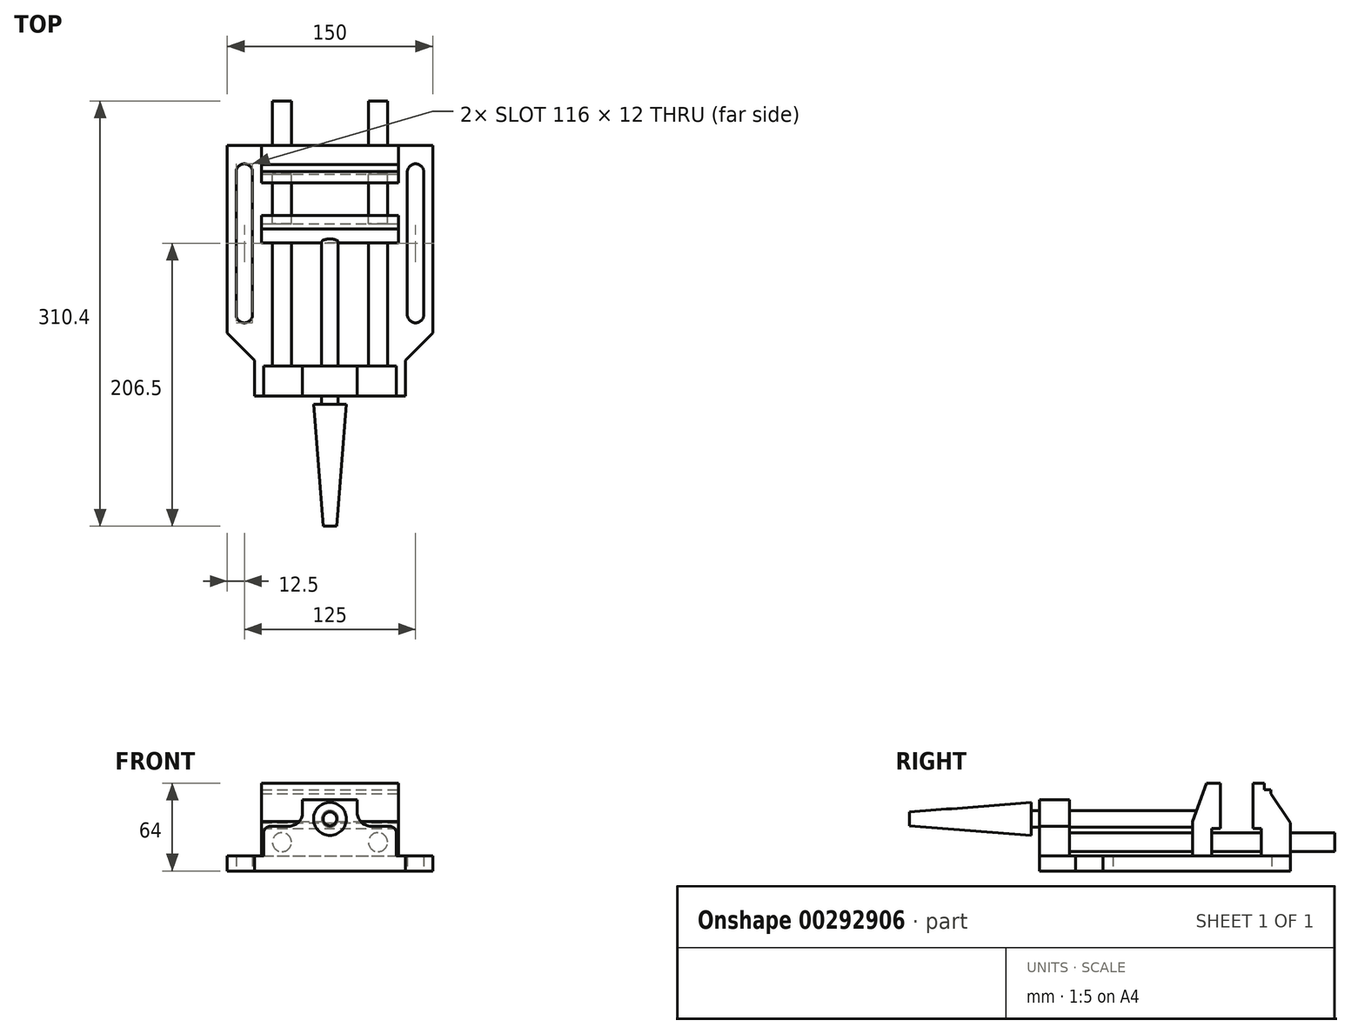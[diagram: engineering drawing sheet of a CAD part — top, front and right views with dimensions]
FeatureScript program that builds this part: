
annotation { "Feature Type Name" : "Feature", "Feature Type Description" : "" }
export const myFeature = defineFeature(function(context is Context, id is Id, definition is map)
    precondition{}
    {
        {
            var Q0;
            Q0=qCreatedBy(makeId("Top.planeOp"),FACE);
            var sketch = newSketch(context, id + "F0", { "sketchPlane" : qUnion([Q0])});
            skLineSegment(sketch, "E0", {"start": v(0, 0) * mm, "end": v(0, 26.2) * mm});
            skLineSegment(sketch, "E1", {"start": v(0, 26.2) * mm, "end": v(20, 46.2) * mm});
            skLineSegment(sketch, "E2", {"start": v(20, 46.2) * mm, "end": v(20, 183) * mm});
            skLineSegment(sketch, "E3", {"start": v(20, 183) * mm, "end": v(-55, 183) * mm});
            skLineSegment(sketch, "E4", {"start": v(-55, 183) * mm, "end": v(-55, 0) * mm});
            skLineSegment(sketch, "E5", {"start": v(-55, 0) * mm, "end": v(0, 0) * mm});
            skLineSegment(sketch, "E6", {"start": v(13.5, 59.5) * mm, "end": v(13.5, 163.5) * mm});
            skArc(sketch, "E7", {"start": v(13.5, 163.5) * mm, "mid": v(7.5, 169.5) * mm, "end": v(1.5, 163.5) * mm});
            skLineSegment(sketch, "E8", {"start": v(1.5, 59.5) * mm, "end": v(1.5, 163.5) * mm});
            skArc(sketch, "E9", {"start": v(1.5, 59.5) * mm, "mid": v(7.5, 53.5) * mm, "end": v(13.5, 59.5) * mm});
            skSolve(sketch);
        }
        {
            var Q0;
            Q0=makeQuery(id+"F0.imprint","IMPRINT",FACE,{"disambiguationData":[TD([[makeQuery(id+"F0.imprint","IMPRINT",EDGE,{"derivedFrom":sQuery(id+"F0.wireOp",EDGE,"E0")}),1.0]])]});
            extrude(context, id + "F1", {"entities" : qUnion([Q0]), "depth" : 11 * mm});
        }
        {
            var Q0;
            Q0=makeQuery(id+"F1.opExtrude","SWEPT_BODY",BODY,{"disambiguationData":[OSD([sQuery(id+"F0.wireOp",EDGE,"E0"),sQuery(id+"F0.wireOp",EDGE,"E1"),sQuery(id+"F0.wireOp",EDGE,"E2"),sQuery(id+"F0.wireOp",EDGE,"E3"),sQuery(id+"F0.wireOp",EDGE,"E4"),sQuery(id+"F0.wireOp",EDGE,"E5"),sQuery(id+"F0.wireOp",EDGE,"E6"),sQuery(id+"F0.wireOp",EDGE,"E7"),sQuery(id+"F0.wireOp",EDGE,"E8"),sQuery(id+"F0.wireOp",EDGE,"E9")])]});
            var Q1;
            Q1=makeQuery(id+"F1.opExtrude","SWEPT_FACE",FACE,{"disambiguationData":[OSD([sQuery(id+"F0.wireOp",EDGE,"E4")])]});
            mirror(context, id + "F2", {"operationType" : NewBodyOperationType.ADD, "entities" : qUnion([Q0]), "mirrorPlane" : qUnion([Q1])});
        }
        {
            var Q0;
            {var subQ0=makeQuery(id+"F1.opExtrude","SWEPT_FACE",FACE,{"disambiguationData":[OSD([sQuery(id+"F0.wireOp",EDGE,"E5")])]});Q0=makeQuery(id+"F2.boolean.opBoolean","MERGE",FACE,{"derivedFrom":[subQ0,makeQuery(id+"F2.opPattern","COPY",FACE,{"derivedFrom":subQ0,"instanceName":"1"})]});}
            var sketch = newSketch(context, id + "F3", { "sketchPlane" : qUnion([Q0])});
            skLineSegment(sketch, "E10", {"start": v(-103.5, 0) * mm, "end": v(-6.5, 0) * mm});
            skLineSegment(sketch, "E11", {"start": v(-6.5, 0) * mm, "end": v(-6.5, 27.6) * mm});
            skLineSegment(sketch, "E12", {"start": v(-11.5, 32.6) * mm, "end": v(-25, 32.6) * mm});
            skLineSegment(sketch, "E13", {"start": v(-35, 42.6) * mm, "end": v(-35, 52) * mm});
            skLineSegment(sketch, "E14", {"start": v(-35, 52) * mm, "end": v(-75, 52) * mm});
            skLineSegment(sketch, "E15", {"start": v(-75, 52) * mm, "end": v(-75, 42.6) * mm});
            skLineSegment(sketch, "E16", {"start": v(-85, 32.6) * mm, "end": v(-98.5, 32.6) * mm});
            skLineSegment(sketch, "E17", {"start": v(-103.5, 27.6) * mm, "end": v(-103.5, 0) * mm});
            skPoint(sketch, "E18.visualSharp", {"position": v(-103.5, 32.6) * mm});
            skArc(sketch, "E18.filletArc", {"start": v(-98.5, 32.6) * mm, "mid": v(-102.04, 31.14) * mm, "end": v(-103.5, 27.6) * mm});
            skPoint(sketch, "E19.visualSharp", {"position": v(-6.5, 32.6) * mm});
            skArc(sketch, "E19.filletArc", {"start": v(-6.5, 27.6) * mm, "mid": v(-7.96, 31.14) * mm, "end": v(-11.5, 32.6) * mm});
            skCircle(sketch, "E20", {"center": v(-55, 38) * mm, "radius": 6 * mm});
            skPoint(sketch, "E21.visualSharp", {"position": v(-75, 32.6) * mm});
            skArc(sketch, "E21.filletArc", {"start": v(-85, 32.6) * mm, "mid": v(-77.93, 35.53) * mm, "end": v(-75, 42.6) * mm});
            skPoint(sketch, "E22.visualSharp", {"position": v(-35, 32.6) * mm});
            skArc(sketch, "E22.filletArc", {"start": v(-35, 42.6) * mm, "mid": v(-32.07, 35.53) * mm, "end": v(-25, 32.6) * mm});
            skSolve(sketch);
        }
        {
            var Q0;
            Q0=makeQuery(id+"F3.imprint","IMPRINT",FACE,{"disambiguationData":[TD([[makeQuery(id+"F3.imprint","IMPRINT",EDGE,{"derivedFrom":sQuery(id+"F3.wireOp",EDGE,"E12")}),1.0]])]});
            extrude(context, id + "F4", {"entities" : qUnion([Q0]), "operationType" : NewBodyOperationType.ADD, "oppositeDirection" : true, "depth" : 22 * mm});
        }
        {
            var Q0;
            Q0=makeQuery(id+"F1.opExtrude","SWEPT_FACE",FACE,{"disambiguationData":[OSD([sQuery(id+"F0.wireOp",EDGE,"E2")])]});
            cPlane(context, id + "F5", {"entities" : qUnion([Q0]), "cplaneType" : CPlaneType.OFFSET, "offset" : 25 * mm, "oppositeDirection" : true, "width" : 150 * mm, "height" : 150 * mm});
        }
        {
            var Q0;
            Q0=qCreatedBy(id+"F5.planeOp",FACE);
            var sketch = newSketch(context, id + "F6", { "sketchPlane" : qUnion([Q0])});
            skLineSegment(sketch, "E23", {"start": v(183, 0) * mm, "end": v(183, 35) * mm});
            skLineSegment(sketch, "E24", {"start": v(183, 35) * mm, "end": v(169, 56.4) * mm});
            skLineSegment(sketch, "E25", {"start": v(169, 56.4) * mm, "end": v(169, 59.4) * mm});
            skLineSegment(sketch, "E26", {"start": v(169, 59.4) * mm, "end": v(164, 59.4) * mm});
            skLineSegment(sketch, "E27", {"start": v(164, 59.4) * mm, "end": v(164, 64) * mm});
            skLineSegment(sketch, "E28", {"start": v(164, 64) * mm, "end": v(155.8, 64) * mm});
            skLineSegment(sketch, "E29", {"start": v(155.8, 64) * mm, "end": v(155.8, 31) * mm});
            skLineSegment(sketch, "E30", {"start": v(155.8, 31) * mm, "end": v(155.8, 31) * mm});
            skLineSegment(sketch, "E31", {"start": v(162, 31) * mm, "end": v(162, 0) * mm});
            skLineSegment(sketch, "E32", {"start": v(162, 0) * mm, "end": v(183, 0) * mm});
            skLineSegment(sketch, "E33", {"start": v(155.8, 31) * mm, "end": v(162, 31) * mm});
            skSolve(sketch);
        }
        {
            var Q0;
            Q0=makeQuery(id+"F6.imprint","IMPRINT",FACE,{"disambiguationData":[TD([[makeQuery(id+"F6.imprint","IMPRINT",EDGE,{"derivedFrom":sQuery(id+"F6.wireOp",EDGE,"E23")}),1.0]])]});
            extrude(context, id + "F7", {"entities" : qUnion([Q0]), "operationType" : NewBodyOperationType.ADD, "oppositeDirection" : true, "depth" : 100 * mm});
        }
        {
            var Q0;
            {var subQ0=makeQuery(id+"F1.opExtrude","SWEPT_FACE",FACE,{"disambiguationData":[OSD([sQuery(id+"F0.wireOp",EDGE,"E3")])]});Q0=makeQuery(id+"F7.boolean.opBoolean","MERGE",FACE,{"derivedFrom":[makeQuery(id+"F2.boolean.opBoolean","MERGE",FACE,{"derivedFrom":[subQ0,makeQuery(id+"F2.opPattern","COPY",FACE,{"derivedFrom":subQ0,"instanceName":"1"})]}),makeQuery(id+"F7.opExtrude","SWEPT_FACE",FACE,{"disambiguationData":[OSD([sQuery(id+"F6.wireOp",EDGE,"E23")])]})]});}
            var sketch = newSketch(context, id + "F8", { "sketchPlane" : qUnion([Q0])});
            skCircle(sketch, "E34", {"center": v(19.95, 21) * mm, "radius": 6.95 * mm});
            skCircle(sketch, "E35", {"center": v(90.05, 21) * mm, "radius": 6.95 * mm});
            skLineSegment(sketch, "E36", {"start": v(55, 0) * mm, "end": v(55, 13.98) * mm});
            skSolve(sketch);
        }
        {
            var Q0;
            Q0=makeQuery(id+"F8.imprint","IMPRINT",FACE,{"disambiguationData":[TD([[makeQuery(id+"F8.imprint","IMPRINT",EDGE,{"derivedFrom":sQuery(id+"F8.wireOp",EDGE,"E34")}),1.0]])]});
            var Q1;
            Q1=makeQuery(id+"F8.imprint","IMPRINT",FACE,{"disambiguationData":[TD([[makeQuery(id+"F8.imprint","IMPRINT",EDGE,{"derivedFrom":sQuery(id+"F8.wireOp",EDGE,"E35")}),1.0]])]});
            extrude(context, id + "F9", {"entities" : qUnion([Q0, Q1]), "operationType" : NewBodyOperationType.ADD, "depth" : 32.4 * mm});
        }
        {
            var Q0;
            Q0 = qSketchRegion(id + "F8", true);
            extrude(context, id + "F10", {"entities" : qUnion([Q0]), "operationType" : NewBodyOperationType.ADD, "oppositeDirection" : true, "depth" : 183 * mm});
        }
        {
            var Q0;
            Q0=makeQuery(id+"F1.opExtrude","SWEPT_FACE",FACE,{"disambiguationData":[OSD([sQuery(id+"F0.wireOp",EDGE,"E2")])]});
            cPlane(context, id + "F11", {"entities" : qUnion([Q0]), "cplaneType" : CPlaneType.OFFSET, "offset" : 75 * mm, "oppositeDirection" : true, "width" : 150 * mm, "height" : 150 * mm});
        }
        {
            var Q0;
            Q0=qCreatedBy(id+"F11.planeOp",FACE);
            var sketch = newSketch(context, id + "F12", { "sketchPlane" : qUnion([Q0])});
            skLineSegment(sketch, "E37", {"start": v(0, 38) * mm, "end": v(-95, 38) * mm});
            skLineSegment(sketch, "E38", {"start": v(-95, 38) * mm, "end": v(-95, 33) * mm});
            skLineSegment(sketch, "E39", {"start": v(-95, 33) * mm, "end": v(-6, 26) * mm});
            skLineSegment(sketch, "E40", {"start": v(-6, 26) * mm, "end": v(-6, 32) * mm});
            skLineSegment(sketch, "E41", {"start": v(-6, 32) * mm, "end": v(0, 32) * mm});
            skLineSegment(sketch, "E42", {"start": v(0, 32) * mm, "end": v(0, 38) * mm});
            skLineSegment(sketch, "E43", {"start": v(0, 32) * mm, "end": v(115.38, 32) * mm});
            skLineSegment(sketch, "E44", {"start": v(115.38, 32) * mm, "end": v(115.38, 38) * mm});
            skLineSegment(sketch, "E45", {"start": v(115.38, 38) * mm, "end": v(0, 38) * mm});
            skSolve(sketch);
        }
        {
            var Q0;
            Q0 = qSketchRegion(id + "F12", true);
            var Q1;
            Q1=sQuery(id+"F12.wireOp",EDGE,"E37");
            revolve(context, id + "F13", {"entities" : qUnion([Q0]), "axis" : qUnion([Q1]), "revolveType" : RevolveType.FULL});
        }
        {
            var Q0;
            Q0=makeQuery(id+"F7.opExtrude","CAP_FACE",FACE,{"disambiguationData":[OSD([sQuery(id+"F6.wireOp",EDGE,"E23"),sQuery(id+"F6.wireOp",EDGE,"E24"),sQuery(id+"F6.wireOp",EDGE,"E25"),sQuery(id+"F6.wireOp",EDGE,"E26"),sQuery(id+"F6.wireOp",EDGE,"E27"),sQuery(id+"F6.wireOp",EDGE,"E28"),sQuery(id+"F6.wireOp",EDGE,"E29"),sQuery(id+"F6.wireOp",EDGE,"E31"),sQuery(id+"F6.wireOp",EDGE,"E32"),sQuery(id+"F6.wireOp",EDGE,"E33")])],"isStart":true});
            var sketch = newSketch(context, id + "F14", { "sketchPlane" : qUnion([Q0])});
            skLineSegment(sketch, "E46", {"start": v(132, 64) * mm, "end": v(132, 31) * mm});
            skLineSegment(sketch, "E47", {"start": v(132, 31) * mm, "end": v(125.8, 31) * mm});
            skLineSegment(sketch, "E48", {"start": v(125.8, 31) * mm, "end": v(125.8, 11) * mm});
            skLineSegment(sketch, "E49", {"start": v(125.8, 11) * mm, "end": v(111.8, 11) * mm});
            skLineSegment(sketch, "E50", {"start": v(111.8, 11) * mm, "end": v(111.8, 35.98) * mm});
            skLineSegment(sketch, "E51", {"start": v(111.8, 35.98) * mm, "end": v(122, 64) * mm});
            skLineSegment(sketch, "E52", {"start": v(122, 64) * mm, "end": v(132, 64) * mm});
            skSolve(sketch);
        }
        {
            var Q0;
            Q0=makeQuery(id+"F14.imprint","IMPRINT",FACE,{"disambiguationData":[TD([[makeQuery(id+"F14.imprint","IMPRINT",EDGE,{"derivedFrom":sQuery(id+"F14.wireOp",EDGE,"E46")}),-1.0]])]});
            extrude(context, id + "F15", {"entities" : qUnion([Q0]), "operationType" : NewBodyOperationType.ADD, "oppositeDirection" : true, "depth" : 100 * mm});
        }
    });
